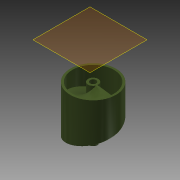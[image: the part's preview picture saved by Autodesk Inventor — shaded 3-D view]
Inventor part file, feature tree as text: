
AUTODESK INVENTOR PART (.ipt)
format: ipt  version: 2014 SP2 (Build 180246200, 246)  size: 261,120 bytes
history: native  units: mm
features: sketch x4, extrude x3, fillet x3, helix x1, plane x1, projected_geometry x1
ambient origin geometry x8: Origin, YZ Plane, XZ Plane, XY Plane, X Axis, Y Axis, Z Axis, Center Point
bodies: Solid1 (feature_tree)
feature tree (13):
  extrude  "Extrusion1"  Depth=3.0mm
  helix  "Coil2"  [1 undecoded]
  plane  "Work Plane1"
  extrude  "Extrusion4"  Depth=3.0mm
  fillet  "Fillet1"  [1 undecoded]
  fillet  "Fillet2"  Radius=47.0mm
  fillet  "Fillet3"  Radius=3.0mm
  extrude  "Extrusion5"  Depth=3.0mm TaperAngle=0.0deg
  sketch  "Sketch1"  dims[d0=8.5mm d1=3.0mm d2=78.0mm d3=0.0mm]
  sketch  "Sketch3"  dims[d17=25.5mm d18=3.0mm]
  projected_geometry  "Projected Loop1"
  sketch  "Sketch6"  dims[d19=50.0mm d20=10.0mm d21=15.0mm d22=0.0mm d23=90.0deg d24=90.0deg d25=0.0mm d26=0.0mm d29=0.0mm d32=47.0mm d33=3.0mm]
  sketch  "Sketch7"  dims[d34=80.0mm d35=50.0mm d36=0.0mm d37=0.5mm d38=1.3mm d39=1.3mm d40=3.0mm d41=0.0mm]
note: 2 required parameter values undecoded (feature->parameter linkage not recoverable at this tier; creation-order binding heuristic only, values carry confidence <= 0.55)
